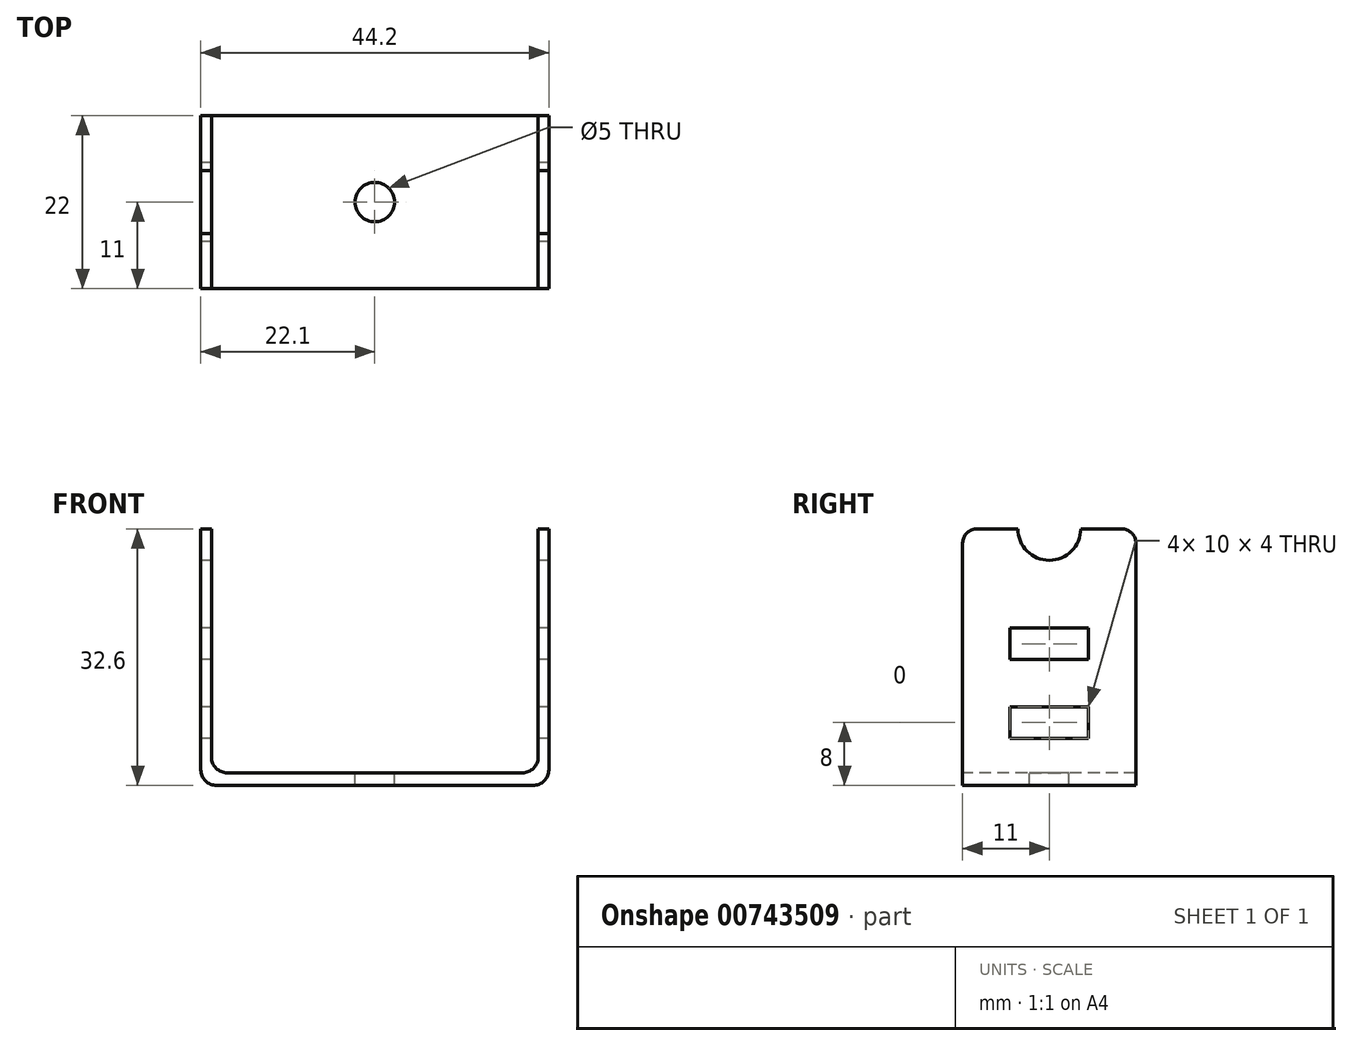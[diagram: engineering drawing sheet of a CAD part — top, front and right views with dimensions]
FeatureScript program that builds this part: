
annotation { "Feature Type Name" : "Feature", "Feature Type Description" : "" }
export const myFeature = defineFeature(function(context is Context, id is Id, definition is map)
    precondition{}
    {
        {
            var Q0;
            Q0=qCreatedBy(makeId("Right.planeOp"),FACE);
            var sketch = newSketch(context, id + "F0", { "sketchPlane" : qUnion([Q0])});
            skLineSegment(sketch, "E0.bottom", {"start": v(-11, 0) * mm, "end": v(11, 0) * mm});
            skLineSegment(sketch, "E0.top", {"start": v(-9.17, 32.6) * mm, "end": v(-4, 32.6) * mm});
            skLineSegment(sketch, "E0.left", {"start": v(-11, 0) * mm, "end": v(-11, 30.77) * mm});
            skLineSegment(sketch, "E0.right", {"start": v(11, 0) * mm, "end": v(11, 30.77) * mm});
            skLineSegment(sketch, "E1.bottom", {"start": v(-5, 10) * mm, "end": v(5, 10) * mm});
            skLineSegment(sketch, "E1.top", {"start": v(-5, 6) * mm, "end": v(5, 6) * mm});
            skLineSegment(sketch, "E1.left", {"start": v(-5, 10) * mm, "end": v(-5, 6) * mm});
            skLineSegment(sketch, "E1.right", {"start": v(5, 10) * mm, "end": v(5, 6) * mm});
            skLineSegment(sketch, "E2.0.1.0", {"start": v(-5, 16) * mm, "end": v(5, 16) * mm});
            skLineSegment(sketch, "E2.0.1.1", {"start": v(5, 20) * mm, "end": v(5, 16) * mm});
            skLineSegment(sketch, "E2.0.1.2", {"start": v(-5, 20) * mm, "end": v(5, 20) * mm});
            skLineSegment(sketch, "E2.0.1.3", {"start": v(-5, 20) * mm, "end": v(-5, 16) * mm});
            skLineSegment(sketch, "E2.direction1", {"start": v(-5, 6) * mm, "end": v(17, 6) * mm, "construction": true});
            skLineSegment(sketch, "E2.direction2", {"start": v(-5, 6) * mm, "end": v(-5, 16) * mm, "construction": true});
            skArc(sketch, "E3", {"start": v(-4, 32.6) * mm, "mid": v(0, 28.6) * mm, "end": v(4, 32.6) * mm});
            skLineSegment(sketch, "E4.trimOffspring", {"start": v(4, 32.6) * mm, "end": v(9.17, 32.6) * mm});
            skPoint(sketch, "E5.visualSharp", {"position": v(-11, 32.6) * mm});
            skArc(sketch, "E5.filletArc", {"start": v(-9.17, 32.6) * mm, "mid": v(-10.46, 32.06) * mm, "end": v(-11, 30.77) * mm});
            skPoint(sketch, "E6.visualSharp", {"position": v(11, 32.6) * mm});
            skArc(sketch, "E6.filletArc", {"start": v(11, 30.77) * mm, "mid": v(10.46, 32.06) * mm, "end": v(9.17, 32.6) * mm});
            skSolve(sketch);
        }
        {
            var Q0;
            Q0=qSketchRegion(id+"F0",true);
            extrude(context, id + "F1", {"entities" : qUnion([Q0]), "endBound" : BoundingType.SYMMETRIC, "depth" : 44.2 * mm});
        }
        {
            var Q0;
            Q0=makeQuery(id+"F1.opExtrude","SWEPT_FACE",FACE,{"disambiguationData":[OSD([sQuery(id+"F0.wireOp",EDGE,"E0.top")])]});
            var sketch = newSketch(context, id + "F2", { "sketchPlane" : qUnion([Q0])});
            skLineSegment(sketch, "E7.bottom", {"start": v(-20.75, 21.18) * mm, "end": v(20.75, 21.18) * mm});
            skLineSegment(sketch, "E7.top", {"start": v(-20.75, -22.3) * mm, "end": v(20.75, -22.3) * mm});
            skLineSegment(sketch, "E7.left", {"start": v(-20.75, 21.18) * mm, "end": v(-20.75, -22.3) * mm});
            skLineSegment(sketch, "E7.right", {"start": v(20.75, 21.18) * mm, "end": v(20.75, -22.3) * mm});
            skSolve(sketch);
        }
        {
            var Q0;
            Q0=qSketchRegion(id+"F2",true);
            extrude(context, id + "F3", {"entities" : qUnion([Q0]), "operationType" : NewBodyOperationType.REMOVE, "oppositeDirection" : true, "depth" : (32.5 - 1.5) * mm});
        }
        {
            var Q0;
            Q0=makeQuery(id+"F1.opExtrude","CAP_EDGE",EDGE,{"disambiguationData":[OSD([sQuery(id+"F0.wireOp",EDGE,"E0.bottom")])],"isStart":true});
            fillet(context, id + "F4", {"entities" : qUnion([Q0]), "radius" : 2 * mm, "tangentPropagation" : true, "allowEdgeOverflow" : false});
        }
        {
            var Q0;
            Q0=makeQuery(id+"F1.opExtrude","CAP_EDGE",EDGE,{"disambiguationData":[OSD([sQuery(id+"F0.wireOp",EDGE,"E0.bottom")])],"isStart":false});
            var Q1;
            Q1=makeQuery(id+"F3.boolean.opBoolean","COPY",EDGE,{"derivedFrom":makeQuery(id+"F3.opExtrude","CAP_EDGE",EDGE,{"disambiguationData":[OSD([sQuery(id+"F2.wireOp",EDGE,"E7.left")])],"isStart":false})});
            var Q2;
            Q2=makeQuery(id+"F3.boolean.opBoolean","COPY",EDGE,{"derivedFrom":makeQuery(id+"F3.opExtrude","CAP_EDGE",EDGE,{"disambiguationData":[OSD([sQuery(id+"F2.wireOp",EDGE,"E7.right")])],"isStart":false})});
            fillet(context, id + "F5", {"entities" : qUnion([Q0, Q1, Q2]), "radius" : 2 * mm, "tangentPropagation" : true, "allowEdgeOverflow" : false});
        }
        {
            var Q0;
            Q0=makeQuery(id+"F3.boolean.opBoolean","COPY",FACE,{"derivedFrom":makeQuery(id+"F3.opExtrude","CAP_FACE",FACE,{"disambiguationData":[OSD([sQuery(id+"F2.wireOp",EDGE,"E7.bottom"),sQuery(id+"F2.wireOp",EDGE,"E7.top"),sQuery(id+"F2.wireOp",EDGE,"E7.left"),sQuery(id+"F2.wireOp",EDGE,"E7.right")])],"isStart":false})});
            var sketch = newSketch(context, id + "F6", { "sketchPlane" : qUnion([Q0])});
            skCircle(sketch, "E8", {"center": v(0, 0) * mm, "radius": 2.5 * mm});
            skSolve(sketch);
        }
        {
            var Q0;
            Q0=qSketchRegion(id+"F6",true);
            extrude(context, id + "F7", {"entities" : qUnion([Q0]), "operationType" : NewBodyOperationType.REMOVE, "oppositeDirection" : true, "depth" : 25 * mm});
        }
    });
